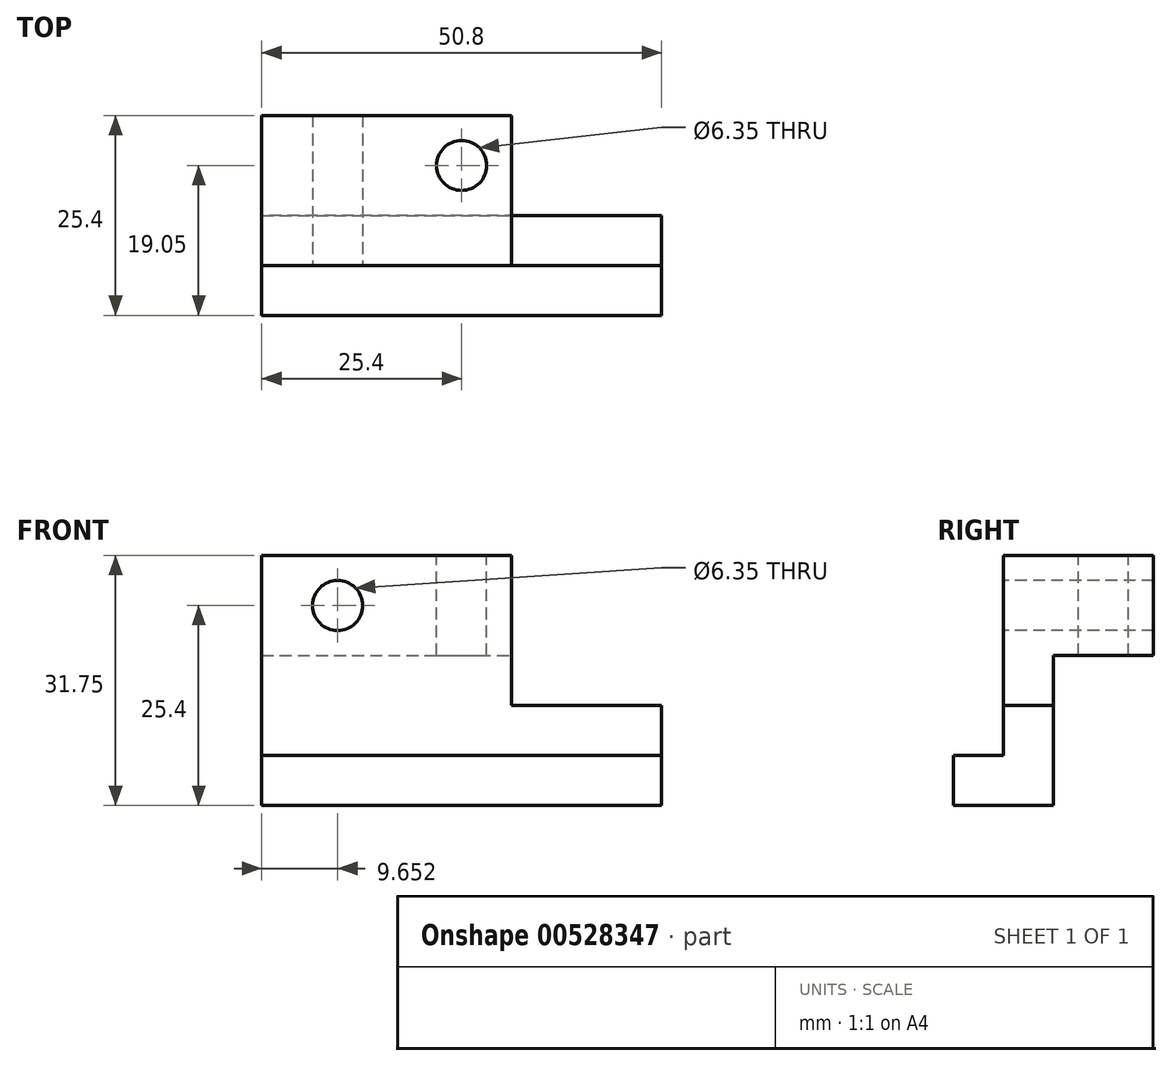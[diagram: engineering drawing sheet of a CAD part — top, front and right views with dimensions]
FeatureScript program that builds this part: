
annotation { "Feature Type Name" : "Feature", "Feature Type Description" : "" }
export const myFeature = defineFeature(function(context is Context, id is Id, definition is map)
    precondition{}
    {
        {
            var Q0;
            Q0=qCreatedBy(makeId("Front.planeOp"),FACE);
            var sketch = newSketch(context, id + "F0", { "sketchPlane" : qUnion([Q0])});
            skLineSegment(sketch, "E0", {"start": v(0, 6.35) * mm, "end": v(19.05, 6.35) * mm});
            skLineSegment(sketch, "E1", {"start": v(19.05, 6.35) * mm, "end": v(19.05, -6.35) * mm});
            skLineSegment(sketch, "E2", {"start": v(19.05, -6.35) * mm, "end": v(-31.75, -6.35) * mm});
            skLineSegment(sketch, "E3", {"start": v(-31.75, -6.35) * mm, "end": v(-31.75, 25.4) * mm});
            skLineSegment(sketch, "E4", {"start": v(-31.75, 25.4) * mm, "end": v(0, 25.4) * mm});
            skLineSegment(sketch, "E5", {"start": v(0, 25.4) * mm, "end": v(0, 6.35) * mm});
            skLineSegment(sketch, "E6", {"start": v(-31.75, 0) * mm, "end": v(19.05, 0) * mm});
            skCircle(sketch, "E7", {"center": v(-22.1, 19.05) * mm, "radius": 3.18 * mm});
            skLineSegment(sketch, "E8", {"start": v(-31.75, 12.7) * mm, "end": v(0, 12.7) * mm});
            skSolve(sketch);
        }
        {
            var Q0;
            {var subQ1=sQuery(id+"F0.wireOp",EDGE,"E0");Q0=makeQuery(id+"F0.imprint","IMPRINT",FACE,{"disambiguationData":[TD([[makeQuery(id+"F0.imprint","IMPRINT",EDGE,{"derivedFrom":subQ1}),-1.0]])]});}
            extrude(context, id + "F1", {"entities" : qUnion([Q0]), "oppositeDirection" : true, "depth" : 6.35 * mm, "offsetDistance" : 25.4 * mm});
        }
        {
            var Q0;
            Q0=qCreatedBy(makeId("Front.planeOp"),FACE);
            var sketch = newSketch(context, id + "F2", { "sketchPlane" : qUnion([Q0])});
            skLineSegment(sketch, "E9", {"start": v(0, 6.35) * mm, "end": v(19.05, 6.35) * mm});
            skLineSegment(sketch, "E10", {"start": v(19.05, 6.35) * mm, "end": v(19.05, -6.35) * mm});
            skLineSegment(sketch, "E11", {"start": v(19.05, -6.35) * mm, "end": v(-31.75, -6.35) * mm});
            skLineSegment(sketch, "E12", {"start": v(-31.75, -6.35) * mm, "end": v(-31.75, 25.4) * mm});
            skLineSegment(sketch, "E13", {"start": v(-31.75, 25.4) * mm, "end": v(0, 25.4) * mm});
            skLineSegment(sketch, "E14", {"start": v(0, 25.4) * mm, "end": v(0, 6.35) * mm});
            skLineSegment(sketch, "E15", {"start": v(-31.75, 0) * mm, "end": v(19.05, 0) * mm});
            skCircle(sketch, "E16", {"center": v(-22.1, 19.05) * mm, "radius": 3.18 * mm});
            skLineSegment(sketch, "E17", {"start": v(-31.75, 12.7) * mm, "end": v(0, 12.7) * mm});
            skSolve(sketch);
        }
        {
            var Q0;
            {var subQ0=sQuery(id+"F2.wireOp",EDGE,"E11");Q0=makeQuery(id+"F2.imprint","IMPRINT",FACE,{"disambiguationData":[TD([[makeQuery(id+"F2.imprint","IMPRINT",EDGE,{"derivedFrom":subQ0}),-1.0]])]});}
            extrude(context, id + "F3", {"entities" : qUnion([Q0]), "operationType" : NewBodyOperationType.ADD, "endBound" : BoundingType.SYMMETRIC, "depth" : 12.7 * mm, "offsetDistance" : 25.4 * mm});
        }
        {
            var Q0;
            Q0=qCreatedBy(makeId("Front.planeOp"),FACE);
            var sketch = newSketch(context, id + "F4", { "sketchPlane" : qUnion([Q0])});
            skLineSegment(sketch, "E18", {"start": v(0, 6.35) * mm, "end": v(19.05, 6.35) * mm});
            skLineSegment(sketch, "E19", {"start": v(19.05, 6.35) * mm, "end": v(19.05, -6.35) * mm});
            skLineSegment(sketch, "E20", {"start": v(19.05, -6.35) * mm, "end": v(-31.75, -6.35) * mm});
            skLineSegment(sketch, "E21", {"start": v(-31.75, -6.35) * mm, "end": v(-31.75, 25.4) * mm});
            skLineSegment(sketch, "E22", {"start": v(-31.75, 25.4) * mm, "end": v(0, 25.4) * mm});
            skLineSegment(sketch, "E23", {"start": v(0, 25.4) * mm, "end": v(0, 6.35) * mm});
            skLineSegment(sketch, "E24", {"start": v(-31.75, 0) * mm, "end": v(19.05, 0) * mm});
            skCircle(sketch, "E25", {"center": v(-22.1, 19.05) * mm, "radius": 3.18 * mm});
            skLineSegment(sketch, "E26", {"start": v(-31.75, 12.7) * mm, "end": v(-21.65, 12.7) * mm});
            skLineSegment(sketch, "E27", {"start": v(-31.75, 12.7) * mm, "end": v(0, 12.7) * mm});
            skPoint(sketch, "E27.endSnap0", {"position": v(-26.7, 12.7) * mm});
            skSolve(sketch);
        }
        {
            var Q0;
            {var subQ1=sQuery(id+"F4.wireOp",EDGE,"E22");Q0=makeQuery(id+"F4.imprint","IMPRINT",FACE,{"disambiguationData":[TD([[makeQuery(id+"F4.imprint","IMPRINT",EDGE,{"derivedFrom":subQ1}),-1.0]])]});}
            extrude(context, id + "F5", {"entities" : qUnion([Q0]), "operationType" : NewBodyOperationType.ADD, "oppositeDirection" : true, "depth" : 19.05 * mm, "offsetDistance" : 25.4 * mm});
        }
        {
            var Q0;
            Q0=makeQuery(id+"F5.opExtrude","SWEPT_FACE",FACE,{"disambiguationData":[OSD([sQuery(id+"F4.wireOp",EDGE,"E22")])]});
            var sketch = newSketch(context, id + "F6", { "sketchPlane" : qUnion([Q0])});
            skCircle(sketch, "E28", {"center": v(-6.35, 12.7) * mm, "radius": 3.18 * mm});
            skSolve(sketch);
        }
        {
            var Q0;
            Q0=makeQuery(id+"F6.imprint","IMPRINT",FACE,{"disambiguationData":[TD([[makeQuery(id+"F6.imprint","IMPRINT",EDGE,{"derivedFrom":sQuery(id+"F6.wireOp",EDGE,"E28")}),1.0]])]});
            extrude(context, id + "F7", {"entities" : qUnion([Q0]), "operationType" : NewBodyOperationType.REMOVE, "endBound" : BoundingType.THROUGH_ALL, "oppositeDirection" : true, "depth" : 25.4 * mm, "offsetDistance" : 25.4 * mm});
        }
    });
